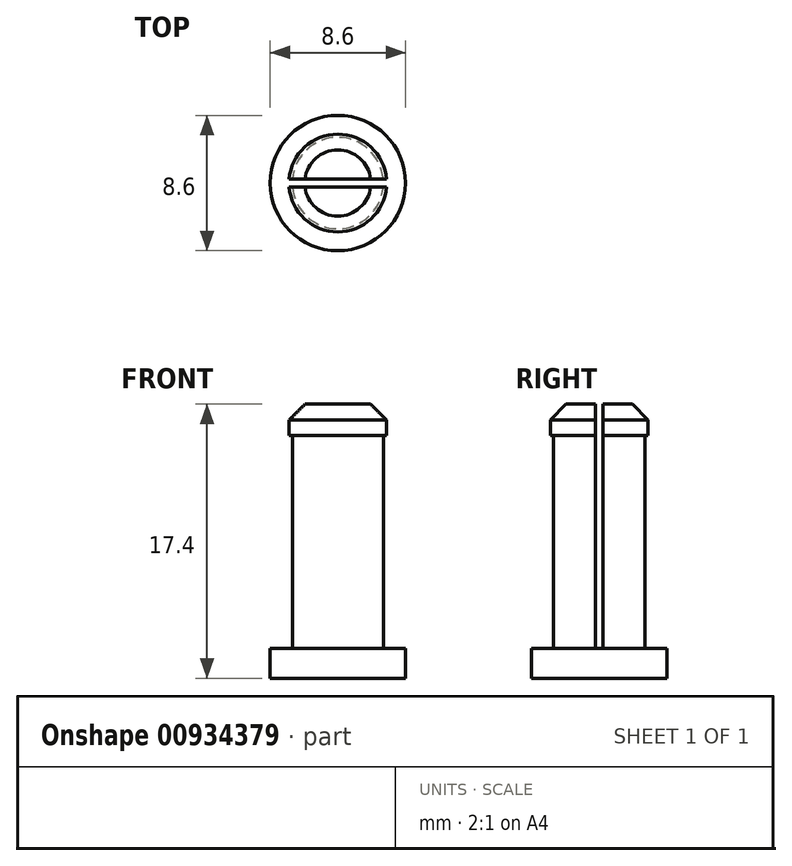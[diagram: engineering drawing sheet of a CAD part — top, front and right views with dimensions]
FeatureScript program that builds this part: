
annotation { "Feature Type Name" : "Feature", "Feature Type Description" : "" }
export const myFeature = defineFeature(function(context is Context, id is Id, definition is map)
    precondition{}
    {
        {
            var Q0;
            Q0=qCreatedBy(makeId("Top.planeOp"),FACE);
            var sketch = newSketch(context, id + "F0", { "sketchPlane" : qUnion([Q0])});
            skCircle(sketch, "E0", {"center": v(0, 0) * mm, "radius": 4.3 * mm});
            skCircle(sketch, "E1", {"center": v(0, 0) * mm, "radius": 2.9 * mm});
            skLineSegment(sketch, "E2", {"start": v(0, 0) * mm, "end": v(-5.8, 0) * mm, "construction": true});
            skLineSegment(sketch, "E3", {"start": v(0, 0) * mm, "end": v(5.92, 0) * mm, "construction": true});
            skLineSegment(sketch, "E4.0", {"start": v(0, 0.25) * mm, "end": v(-5.8, 0.25) * mm});
            skLineSegment(sketch, "E4.1", {"start": v(0, 0.25) * mm, "end": v(5.92, 0.25) * mm});
            skLineSegment(sketch, "E5.0", {"start": v(0, -0.25) * mm, "end": v(-5.8, -0.25) * mm});
            skLineSegment(sketch, "E5.1", {"start": v(0, -0.25) * mm, "end": v(5.92, -0.25) * mm});
            skSolve(sketch);
        }
        {
            var Q0;
            {var subQ0=sQuery(id+"F0.wireOp",EDGE,"E4.0");var subQ1=sQuery(id+"F0.wireOp",EDGE,"E0");var subQ2=makeQuery(id+"F0.imprint","INTERSECT",VERTEX,{"derivedFrom":[subQ1,subQ0]});Q0=makeQuery(id+"F0.imprint","IMPRINT",FACE,{"disambiguationData":[TD([[makeQuery(id+"F0.imprint","IMPRINT",EDGE,{"disambiguationData":[TD([[subQ2,1.0]])],"derivedFrom":subQ1}),1.0]])]});}
            var Q1;
            {var subQ0=sQuery(id+"F0.wireOp",EDGE,"E4.0");var subQ1=sQuery(id+"F0.wireOp",EDGE,"E1");var subQ2=makeQuery(id+"F0.imprint","INTERSECT",VERTEX,{"derivedFrom":[subQ1,subQ0]});Q1=makeQuery(id+"F0.imprint","IMPRINT",FACE,{"disambiguationData":[TD([[makeQuery(id+"F0.imprint","IMPRINT",EDGE,{"disambiguationData":[TD([[subQ2,1.0]])],"derivedFrom":subQ1}),1.0]])]});}
            var Q2;
            {var subQ0=sQuery(id+"F0.wireOp",EDGE,"E4.0");var subQ1=sQuery(id+"F0.wireOp",EDGE,"E0");var subQ2=makeQuery(id+"F0.imprint","INTERSECT",VERTEX,{"derivedFrom":[subQ1,subQ0]});Q2=makeQuery(id+"F0.imprint","IMPRINT",FACE,{"disambiguationData":[TD([[makeQuery(id+"F0.imprint","IMPRINT",EDGE,{"disambiguationData":[TD([[subQ2,-1.0]])],"derivedFrom":subQ1}),1.0]])]});}
            var Q3;
            {var subQ0=sQuery(id+"F0.wireOp",EDGE,"E4.1");var subQ1=sQuery(id+"F0.wireOp",EDGE,"E0");var subQ2=makeQuery(id+"F0.imprint","INTERSECT",VERTEX,{"derivedFrom":[subQ1,subQ0]});Q3=makeQuery(id+"F0.imprint","IMPRINT",FACE,{"disambiguationData":[TD([[makeQuery(id+"F0.imprint","IMPRINT",EDGE,{"disambiguationData":[TD([[subQ2,1.0]])],"derivedFrom":subQ1}),1.0]])]});}
            var Q4;
            {var subQ0=sQuery(id+"F0.wireOp",EDGE,"E5.0");var subQ1=sQuery(id+"F0.wireOp",EDGE,"E0");var subQ2=makeQuery(id+"F0.imprint","INTERSECT",VERTEX,{"derivedFrom":[subQ1,subQ0]});Q4=makeQuery(id+"F0.imprint","IMPRINT",FACE,{"disambiguationData":[TD([[makeQuery(id+"F0.imprint","IMPRINT",EDGE,{"disambiguationData":[TD([[subQ2,-1.0]])],"derivedFrom":subQ1}),1.0]])]});}
            var Q5;
            {var subQ0=sQuery(id+"F0.wireOp",EDGE,"E5.0");var subQ1=sQuery(id+"F0.wireOp",EDGE,"E1");var subQ2=makeQuery(id+"F0.imprint","INTERSECT",VERTEX,{"derivedFrom":[subQ1,subQ0]});Q5=makeQuery(id+"F0.imprint","IMPRINT",FACE,{"disambiguationData":[TD([[makeQuery(id+"F0.imprint","IMPRINT",EDGE,{"disambiguationData":[TD([[subQ2,-1.0]])],"derivedFrom":subQ1}),1.0]])]});}
            var Q6;
            {var subQ1=sQuery(id+"F0.wireOp",EDGE,"E4.0");var subQ3=sQuery(id+"F0.wireOp",EDGE,"E1");var subQ4=makeQuery(id+"F0.imprint","INTERSECT",VERTEX,{"derivedFrom":[subQ3,subQ1]});Q6=makeQuery(id+"F0.imprint","IMPRINT",FACE,{"disambiguationData":[TD([[makeQuery(id+"F0.imprint","IMPRINT",EDGE,{"disambiguationData":[TD([[subQ4,-1.0]])],"derivedFrom":subQ3}),1.0]])]});}
            extrude(context, id + "F1", {"entities" : qUnion([Q0, Q1, Q2, Q3, Q4, Q5, Q6]), "oppositeDirection" : true, "depth" : 1.9 * mm, "offsetDistance" : 25 * mm});
        }
        {
            var Q0;
            {var subQ0=sQuery(id+"F0.wireOp",EDGE,"E5.0");var subQ1=sQuery(id+"F0.wireOp",EDGE,"E1");var subQ2=makeQuery(id+"F0.imprint","INTERSECT",VERTEX,{"derivedFrom":[subQ1,subQ0]});Q0=makeQuery(id+"F0.imprint","IMPRINT",FACE,{"disambiguationData":[TD([[makeQuery(id+"F0.imprint","IMPRINT",EDGE,{"disambiguationData":[TD([[subQ2,-1.0]])],"derivedFrom":subQ1}),1.0]])]});}
            var Q1;
            {var subQ0=sQuery(id+"F0.wireOp",EDGE,"E4.0");var subQ1=sQuery(id+"F0.wireOp",EDGE,"E1");var subQ2=makeQuery(id+"F0.imprint","INTERSECT",VERTEX,{"derivedFrom":[subQ1,subQ0]});Q1=makeQuery(id+"F0.imprint","IMPRINT",FACE,{"disambiguationData":[TD([[makeQuery(id+"F0.imprint","IMPRINT",EDGE,{"disambiguationData":[TD([[subQ2,1.0]])],"derivedFrom":subQ1}),1.0]])]});}
            extrude(context, id + "F2", {"entities" : qUnion([Q0, Q1]), "operationType" : NewBodyOperationType.ADD, "depth" : 13.5 * mm, "offsetDistance" : 25 * mm});
        }
        {
            var Q0;
            Q0=makeQuery(id+"F2.opExtrude","CAP_FACE",FACE,{"disambiguationData":[OSD([sQuery(id+"F0.wireOp",EDGE,"E1"),sQuery(id+"F0.wireOp",EDGE,"E4.0"),sQuery(id+"F0.wireOp",EDGE,"E4.1")])],"isStart":false});
            var sketch = newSketch(context, id + "F3", { "sketchPlane" : qUnion([Q0])});
            skCircle(sketch, "E6", {"center": v(0, 0) * mm, "radius": 3.1 * mm});
            skPoint(sketch, "E7", {"position": v(0, -0.25) * mm});
            skPoint(sketch, "E8", {"position": v(0, 0.25) * mm});
            skLineSegment(sketch, "E9", {"start": v(0, 0.25) * mm, "end": v(-3.09, 0.25) * mm});
            skLineSegment(sketch, "E10", {"start": v(0, 0.25) * mm, "end": v(3.09, 0.25) * mm});
            skLineSegment(sketch, "E11", {"start": v(0, -0.25) * mm, "end": v(-3.09, -0.25) * mm});
            skLineSegment(sketch, "E12", {"start": v(0, -0.25) * mm, "end": v(3.09, -0.25) * mm});
            skSolve(sketch);
        }
        {
            var Q0;
            {var subQ0=sQuery(id+"F3.wireOp",EDGE,"E11");Q0=makeQuery(id+"F3.imprint","IMPRINT",FACE,{"disambiguationData":[TD([[makeQuery(id+"F3.imprint","IMPRINT",EDGE,{"derivedFrom":subQ0}),1.0]])]});}
            var Q1;
            {var subQ1=sQuery(id+"F0.wireOp",EDGE,"E1");var subQ2=makeQuery(id+"F2.opExtrude","CAP_EDGE",EDGE,{"disambiguationData":[OSD([subQ1]),TDD([makeQuery(id+"F0.imprint","IMPRINT",EDGE,{"disambiguationData":[TD([[makeQuery(id+"F0.imprint","INTERSECT",VERTEX,{"derivedFrom":[subQ1,sQuery(id+"F0.wireOp",EDGE,"E4.0")]}),1.0]])],"derivedFrom":subQ1})])],"isStart":false});Q1=makeQuery(id+"F3.imprint","IMPRINT",FACE,{"disambiguationData":[TD([[makeQuery(id+"F3.imprint","IMPRINT",EDGE,{"derivedFrom":subQ2}),1.0]])]});}
            var Q2;
            {var subQ5=sQuery(id+"F0.wireOp",EDGE,"E1");var subQ6=makeQuery(id+"F2.opExtrude","CAP_EDGE",EDGE,{"disambiguationData":[OSD([subQ5]),TDD([makeQuery(id+"F0.imprint","IMPRINT",EDGE,{"disambiguationData":[TD([[makeQuery(id+"F0.imprint","INTERSECT",VERTEX,{"derivedFrom":[subQ5,sQuery(id+"F0.wireOp",EDGE,"E4.0")]}),1.0]])],"derivedFrom":subQ5})])],"isStart":false});Q2=makeQuery(id+"F3.imprint","IMPRINT",FACE,{"disambiguationData":[TD([[makeQuery(id+"F3.imprint","IMPRINT",EDGE,{"derivedFrom":subQ6}),-1.0]])]});}
            extrude(context, id + "F4", {"entities" : qUnion([Q0, Q1, Q2]), "operationType" : NewBodyOperationType.ADD, "depth" : 2 * mm, "offsetDistance" : 25 * mm});
        }
        {
            var Q0;
            {var subQ0=sQuery(id+"F3.wireOp",EDGE,"E6");Q0=makeQuery(id+"F4.opExtrude","CAP_EDGE",EDGE,{"disambiguationData":[OSD([subQ0]),TDD([makeQuery(id+"F3.imprint","IMPRINT",EDGE,{"disambiguationData":[TD([[makeQuery(id+"F3.imprint","INTERSECT",VERTEX,{"derivedFrom":[subQ0,sQuery(id+"F3.wireOp",EDGE,"E9")]}),1.0]])],"derivedFrom":subQ0})])],"isStart":false});}
            var Q1;
            {var subQ0=sQuery(id+"F3.wireOp",EDGE,"E6");Q1=makeQuery(id+"F4.opExtrude","CAP_EDGE",EDGE,{"disambiguationData":[OSD([subQ0]),TDD([makeQuery(id+"F3.imprint","IMPRINT",EDGE,{"disambiguationData":[TD([[makeQuery(id+"F3.imprint","INTERSECT",VERTEX,{"derivedFrom":[subQ0,sQuery(id+"F3.wireOp",EDGE,"E11")]}),-1.0]])],"derivedFrom":subQ0})])],"isStart":false});}
            chamfer(context, id + "F5", {"entities" : qUnion([Q0, Q1]), "width" : 1 * mm, "tangentPropagation" : true});
        }
    });
